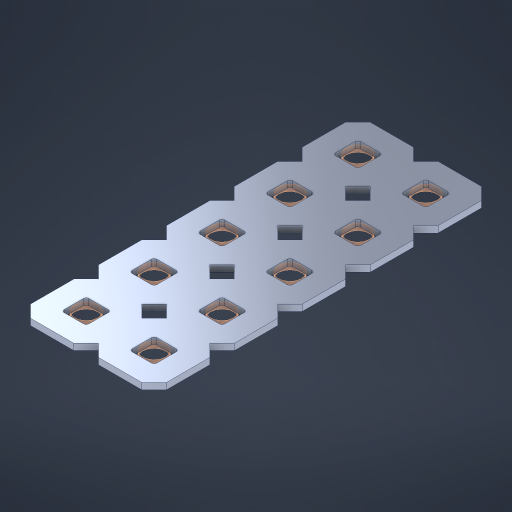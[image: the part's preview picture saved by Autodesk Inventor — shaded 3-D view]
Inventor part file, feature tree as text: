
AUTODESK INVENTOR PART (.ipt)
format: ipt  version: 2023 (Build 270158000, 158)  size: 361,984 bytes
history: native  units: in
note: dims shown in document units (in); Inventor stores cm internally (conversion verified against a paired STEP export)
features: other x11, extrude x9, sketch x2, pattern_linear x1
ambient origin geometry x8: Origin, YZ Plane, XZ Plane, XY Plane, X Axis, Y Axis, Z Axis, Center Point
bodies: Solid1 (feature_tree), Body (feature_tree)
feature tree (23):
  pattern_linear  "Rectangular Pattern1"  Spacing1=0.09in  [1 undecoded]
  sketch  "Sketch1"  dims[d1=0.5in]
  sketch  "Sketch2"  dims[d2=0.182in d3=0.09in d4=0.09in d5=0.09in d6=0.09in d7=0.09in d8=0.09in d9=0.09in d10=0.09in d11=0.02in d13=0.0in d14=0.172in d15=0.0625in d16=0.0in d19=0.5in d22=0.5in]
  other  "Srf1"
  other  "Srf126"
  other  "Srf127"
  other  "Srf128"
  other  "Srf129"
  other  "Srf268"
  other  "Srf269"
  other  "Srf270"
  other  "Srf271"
  other  "Srf272"
  other  "Circle"
  extrude  "ExtrusionSrf126"  Depth=0.09in
  extrude  "ExtrusionSrf127"  Depth=0.09in
  extrude  "ExtrusionSrf128"  Depth=0.09in
  extrude  "ExtrusionSrf129"  Depth=0.09in
  extrude  "ExtrusionSrf268"  Depth=0.09in
  extrude  "ExtrusionSrf269"  Depth=0.09in
  extrude  "ExtrusionSrf270"  Depth=0.09in
  extrude  "ExtrusionSrf271"  Depth=0.02in
  extrude  "ExtrusionSrf272"  TaperAngle=0.0deg  [1 undecoded]
note: 2 required parameter values undecoded (feature->parameter linkage not recoverable at this tier; creation-order binding heuristic only, values carry confidence <= 0.55)
